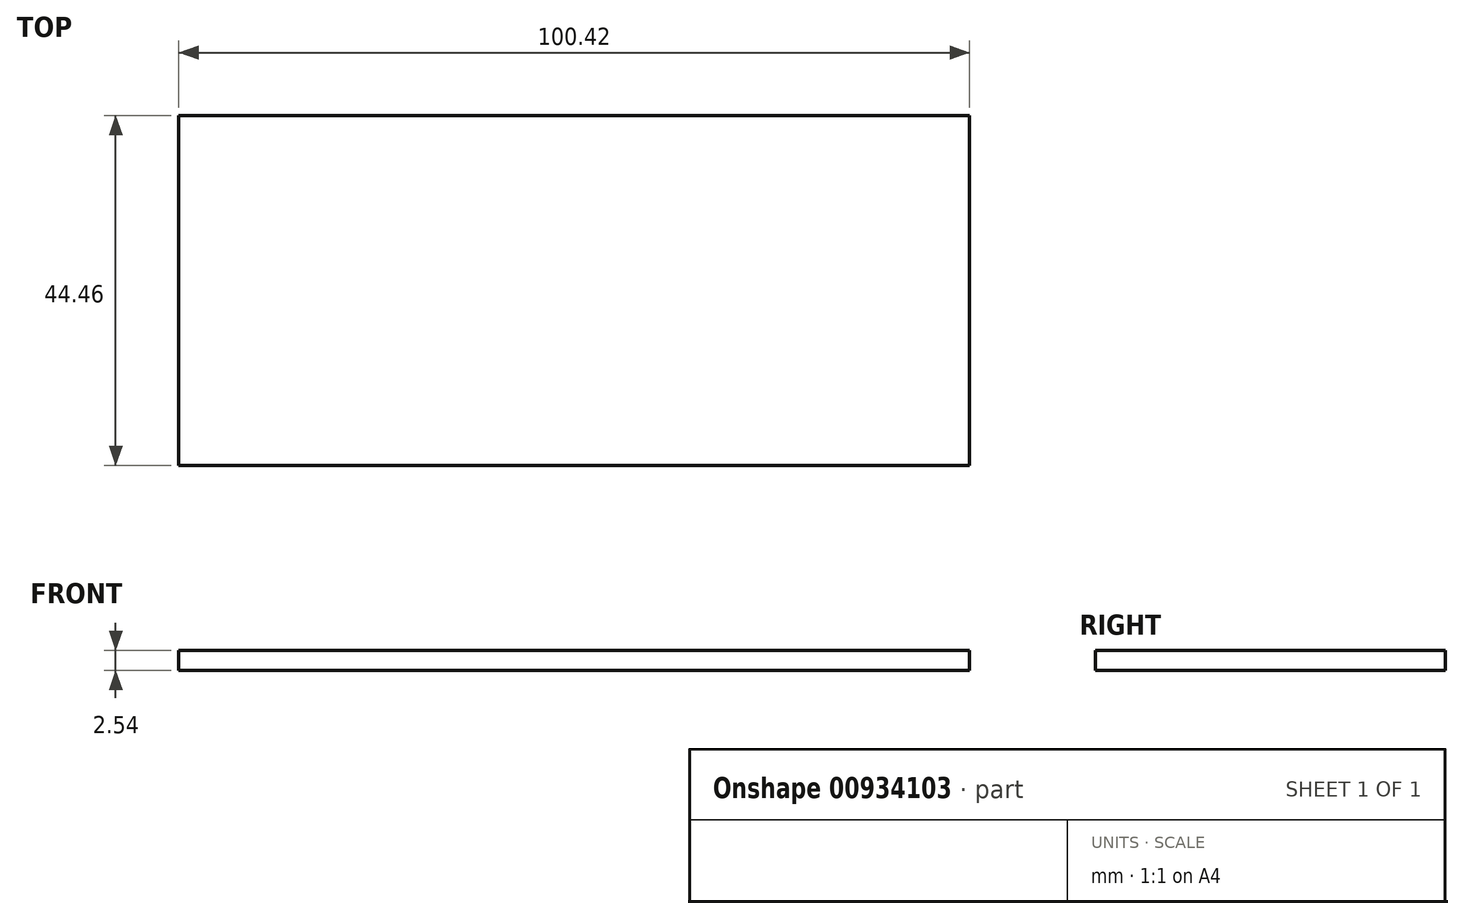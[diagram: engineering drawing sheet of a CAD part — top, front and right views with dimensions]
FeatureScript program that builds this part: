
annotation { "Feature Type Name" : "Feature", "Feature Type Description" : "" }
export const myFeature = defineFeature(function(context is Context, id is Id, definition is map)
    precondition{}
    {
        {
            var Q0;
            Q0=qCreatedBy(makeId("Top.planeOp"),FACE);
            var sketch = newSketch(context, id + "F0", { "sketchPlane" : qUnion([Q0])});
            skLineSegment(sketch, "E0.bottom", {"start": v(50.21, -22.23) * mm, "end": v(-50.21, -22.23) * mm});
            skLineSegment(sketch, "E0.top", {"start": v(50.21, 22.23) * mm, "end": v(-50.21, 22.23) * mm});
            skLineSegment(sketch, "E0.left", {"start": v(50.21, -22.23) * mm, "end": v(50.21, 22.23) * mm});
            skLineSegment(sketch, "E0.right", {"start": v(-50.21, -22.23) * mm, "end": v(-50.21, 22.23) * mm});
            skPoint(sketch, "E0.middle", {"position": v(0, 0) * mm});
            skSolve(sketch);
        }
        {
            var Q0;
            Q0=makeQuery(id+"F0.imprint","IMPRINT",FACE,{"disambiguationData":[TD([[makeQuery(id+"F0.imprint","IMPRINT",EDGE,{"derivedFrom":sQuery(id+"F0.wireOp",EDGE,"E0.bottom")}),-1.0]])]});
            extrude(context, id + "F1", {"entities" : qUnion([Q0]), "depth" : 2.54 * mm, "offsetDistance" : 25.4 * mm});
        }
    });
